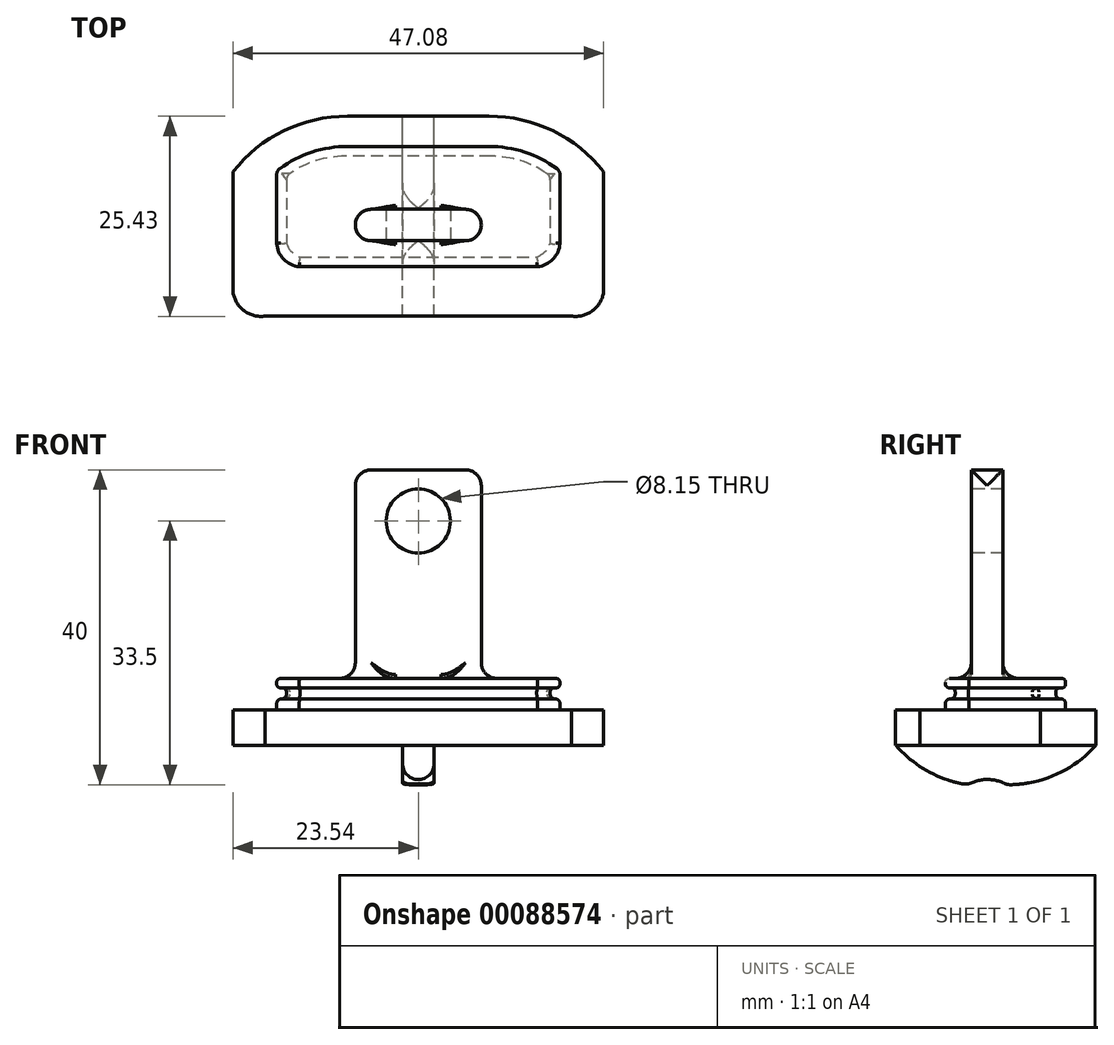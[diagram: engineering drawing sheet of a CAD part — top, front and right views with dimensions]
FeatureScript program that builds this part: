
annotation { "Feature Type Name" : "Feature", "Feature Type Description" : "" }
export const myFeature = defineFeature(function(context is Context, id is Id, definition is map)
    precondition{}
    {
        {
            var Q0;
            Q0=qCreatedBy(makeId("Top.planeOp"),FACE);
            var sketch = newSketch(context, id + "F0", { "sketchPlane" : qUnion([Q0])});
            skLineSegment(sketch, "E0", {"start": v(0, 17.58) * mm, "end": v(9, 17.58) * mm});
            skArc(sketch, "E1", {"start": v(23.54, 10.52) * mm, "mid": v(17.08, 15.72) * mm, "end": v(9, 17.58) * mm});
            skLineSegment(sketch, "E2.MirrorCS", {"start": v(0, 17.58) * mm, "end": v(-9, 17.58) * mm});
            skArc(sketch, "E3.MirrorCS", {"start": v(-23.54, 10.52) * mm, "mid": v(-17.08, 15.72) * mm, "end": v(-9, 17.58) * mm});
            skArc(sketch, "E4", {"start": v(19.44, -7.82) * mm, "mid": v(22.12, -7.14) * mm, "end": v(23.54, -4.76) * mm});
            skArc(sketch, "E5.MirrorCS", {"start": v(-19.44, -7.82) * mm, "mid": v(-22.12, -7.14) * mm, "end": v(-23.54, -4.76) * mm});
            skLineSegment(sketch, "E6", {"start": v(-23.54, 10.52) * mm, "end": v(-23.54, -4.76) * mm});
            skLineSegment(sketch, "E7", {"start": v(-19.44, -7.82) * mm, "end": v(19.44, -7.82) * mm});
            skLineSegment(sketch, "E8", {"start": v(23.54, -4.76) * mm, "end": v(23.54, 10.52) * mm});
            skLineSegment(sketch, "E9", {"start": v(0, 13.64) * mm, "end": v(9, 13.64) * mm});
            skArc(sketch, "E10", {"start": v(18, 10.52) * mm, "mid": v(13.76, 12.84) * mm, "end": v(9, 13.64) * mm});
            skLineSegment(sketch, "E11.MirrorCS", {"start": v(0, 13.64) * mm, "end": v(-9, 13.64) * mm});
            skArc(sketch, "E12.MirrorCS", {"start": v(-18, 10.52) * mm, "mid": v(-13.76, 12.84) * mm, "end": v(-9, 13.64) * mm});
            skArc(sketch, "E13", {"start": v(-18, 1.34) * mm, "mid": v(-17.1, -0.68) * mm, "end": v(-15.12, -1.65) * mm});
            skArc(sketch, "E14.MirrorCS", {"start": v(18, 1.34) * mm, "mid": v(17.1, -0.68) * mm, "end": v(15.12, -1.65) * mm});
            skLineSegment(sketch, "E15", {"start": v(-15.12, -1.65) * mm, "end": v(15.12, -1.65) * mm});
            skLineSegment(sketch, "E16", {"start": v(-18, 1.34) * mm, "end": v(-18, 10.52) * mm});
            skLineSegment(sketch, "E17", {"start": v(18, 10.52) * mm, "end": v(18, 1.34) * mm});
            skSolve(sketch);
        }
        {
            var Q0;
            Q0=makeQuery(id+"F0.imprint","IMPRINT",FACE,{"disambiguationData":[TD([[makeQuery(id+"F0.imprint","IMPRINT",EDGE,{"derivedFrom":sQuery(id+"F0.wireOp",EDGE,"E9")}),-1.0]])]});
            extrude(context, id + "F1", {"entities" : qUnion([Q0]), "depth" : 8.5 * mm});
        }
        {
            var Q0;
            Q0=qCreatedBy(makeId("Top.planeOp"),FACE);
            var sketch = newSketch(context, id + "F2", { "sketchPlane" : qUnion([Q0])});
            skLineSegment(sketch, "E18", {"start": v(0, 11.31) * mm, "end": v(9, 11.31) * mm});
            skArc(sketch, "E19", {"start": v(23.54, 4.25) * mm, "mid": v(17.08, 9.45) * mm, "end": v(9, 11.31) * mm});
            skLineSegment(sketch, "E20.MirrorCS", {"start": v(0, 11.31) * mm, "end": v(-9, 11.31) * mm});
            skArc(sketch, "E21.MirrorCS", {"start": v(-23.54, 4.25) * mm, "mid": v(-17.08, 9.45) * mm, "end": v(-9, 11.31) * mm});
            skArc(sketch, "E22", {"start": v(19.44, -14.09) * mm, "mid": v(22.12, -13.41) * mm, "end": v(23.54, -11.03) * mm});
            skArc(sketch, "E23.MirrorCS", {"start": v(-19.44, -14.09) * mm, "mid": v(-22.12, -13.41) * mm, "end": v(-23.54, -11.03) * mm});
            skLineSegment(sketch, "E24", {"start": v(-23.54, 4.25) * mm, "end": v(-23.54, -11.03) * mm});
            skLineSegment(sketch, "E25", {"start": v(-19.44, -14.09) * mm, "end": v(19.44, -14.09) * mm});
            skLineSegment(sketch, "E26", {"start": v(23.54, -11.03) * mm, "end": v(23.54, 4.25) * mm});
            skSolve(sketch);
        }
        {
            var Q0;
            Q0=makeQuery(id+"F1.opExtrude","SWEPT_BODY",BODY,{"disambiguationData":[OSD([sQuery(id+"F0.wireOp",EDGE,"E0"),sQuery(id+"F0.wireOp",EDGE,"E1"),sQuery(id+"F0.wireOp",EDGE,"E2.MirrorCS"),sQuery(id+"F0.wireOp",EDGE,"E3.MirrorCS"),sQuery(id+"F0.wireOp",EDGE,"E4"),sQuery(id+"F0.wireOp",EDGE,"E5.MirrorCS"),sQuery(id+"F0.wireOp",EDGE,"E6"),sQuery(id+"F0.wireOp",EDGE,"E7"),sQuery(id+"F0.wireOp",EDGE,"E8"),sQuery(id+"F0.wireOp",EDGE,"E9"),sQuery(id+"F0.wireOp",EDGE,"E10"),sQuery(id+"F0.wireOp",EDGE,"E11.MirrorCS"),sQuery(id+"F0.wireOp",EDGE,"E12.MirrorCS"),sQuery(id+"F0.wireOp",EDGE,"E13"),sQuery(id+"F0.wireOp",EDGE,"E14.MirrorCS"),sQuery(id+"F0.wireOp",EDGE,"E15"),sQuery(id+"F0.wireOp",EDGE,"E16"),sQuery(id+"F0.wireOp",EDGE,"E17")])]});
            var Q1;
            Q1=sQuery(id+"F2.wireOp",EDGE,"E26");
            transform(context, id + "F3", {"entities" : qUnion([Q0]), "transformType" : TransformType.TRANSLATION_DISTANCE, "transformDirection" : qUnion([Q1]), "distance" : 6.17 * mm, "oppositeDirection" : true, "makeCopy" : false});
        }
        {
            var Q0;
            Q0=qSketchRegion(id+"F2",true);
            extrude(context, id + "F4", {"entities" : qUnion([Q0]), "operationType" : NewBodyOperationType.ADD, "depth" : 4.5 * mm});
        }
        {
            var Q0;
            Q0=makeQuery(id+"F4.opExtrude","CAP_FACE",FACE,{"disambiguationData":[OSD([sQuery(id+"F2.wireOp",EDGE,"E18"),sQuery(id+"F2.wireOp",EDGE,"E19"),sQuery(id+"F2.wireOp",EDGE,"E20.MirrorCS"),sQuery(id+"F2.wireOp",EDGE,"E21.MirrorCS"),sQuery(id+"F2.wireOp",EDGE,"E22"),sQuery(id+"F2.wireOp",EDGE,"E23.MirrorCS"),sQuery(id+"F2.wireOp",EDGE,"E24"),sQuery(id+"F2.wireOp",EDGE,"E25"),sQuery(id+"F2.wireOp",EDGE,"E26")])],"isStart":false});
            var sketch = newSketch(context, id + "F5", { "sketchPlane" : qUnion([Q0])});
            skLineSegment(sketch, "E27", {"start": v(0, 6.22) * mm, "end": v(-9.3, 6.22) * mm});
            skLineSegment(sketch, "E28", {"start": v(0, -6.57) * mm, "end": v(-15.04, -6.57) * mm});
            skLineSegment(sketch, "E29.MirrorCS", {"start": v(0, 6.22) * mm, "end": v(9.3, 6.22) * mm});
            skLineSegment(sketch, "E30.MirrorCS", {"start": v(0, -6.57) * mm, "end": v(15.04, -6.57) * mm});
            skArc(sketch, "E31", {"start": v(-9.3, 6.22) * mm, "mid": v(-13.23, 5.58) * mm, "end": v(-16.75, 3.73) * mm});
            skArc(sketch, "E32", {"start": v(-16.75, -4.86) * mm, "mid": v(-16.1, -5.9) * mm, "end": v(-15.04, -6.57) * mm});
            skLineSegment(sketch, "E33", {"start": v(-16.75, 3.73) * mm, "end": v(-16.75, -4.86) * mm});
            skLineSegment(sketch, "E34.MirrorCS", {"start": v(16.75, 3.73) * mm, "end": v(16.75, -4.86) * mm});
            skArc(sketch, "E35.MirrorCS", {"start": v(9.3, 6.22) * mm, "mid": v(13.23, 5.58) * mm, "end": v(16.75, 3.73) * mm});
            skArc(sketch, "E36.MirrorCS", {"start": v(16.75, -4.86) * mm, "mid": v(16.1, -5.9) * mm, "end": v(15.04, -6.57) * mm});
            skLineSegment(sketch, "E37.bottom", {"start": v(18.45, -8.13) * mm, "end": v(-18.45, -8.13) * mm});
            skLineSegment(sketch, "E37.top", {"start": v(18.45, 8.13) * mm, "end": v(-18.45, 8.13) * mm});
            skLineSegment(sketch, "E37.left", {"start": v(18.45, -8.13) * mm, "end": v(18.45, 8.13) * mm});
            skLineSegment(sketch, "E37.right", {"start": v(-18.45, -8.13) * mm, "end": v(-18.45, 8.13) * mm});
            skPoint(sketch, "E37.middle", {"position": v(0, 0) * mm});
            skSolve(sketch);
        }
        {
            var Q0;
            Q0=qSketchRegion(id+"F5",true);
            extrude(context, id + "F6", {"entities" : qUnion([Q0]), "operationType" : NewBodyOperationType.REMOVE, "depth" : 2.8 * mm, "hasSecondDirection" : true, "secondDirectionOppositeDirection" : false, "secondDirectionDepth" : 1.4 * mm});
        }
        {
            var Q0;
            Q0=makeQuery(id+"F1.opExtrude","CAP_FACE",FACE,{"disambiguationData":[OSD([sQuery(id+"F0.wireOp",EDGE,"E9"),sQuery(id+"F0.wireOp",EDGE,"E10"),sQuery(id+"F0.wireOp",EDGE,"E11.MirrorCS"),sQuery(id+"F0.wireOp",EDGE,"E12.MirrorCS"),sQuery(id+"F0.wireOp",EDGE,"E13"),sQuery(id+"F0.wireOp",EDGE,"E14.MirrorCS"),sQuery(id+"F0.wireOp",EDGE,"E15"),sQuery(id+"F0.wireOp",EDGE,"E16"),sQuery(id+"F0.wireOp",EDGE,"E17")])],"isStart":false});
            var sketch = newSketch(context, id + "F7", { "sketchPlane" : qUnion([Q0])});
            skLineSegment(sketch, "E38.rect.bottom", {"start": v(8, -4.51) * mm, "end": v(-8, -4.51) * mm});
            skLineSegment(sketch, "E38.rect.top", {"start": v(8, -0.51) * mm, "end": v(-8, -0.51) * mm});
            skLineSegment(sketch, "E38.rect.left", {"start": v(8, -4.51) * mm, "end": v(8, -0.51) * mm});
            skLineSegment(sketch, "E38.rect.right", {"start": v(-8, -4.51) * mm, "end": v(-8, -0.51) * mm});
            skPoint(sketch, "E38.rect.middle", {"position": v(0, -2.51) * mm});
            skSolve(sketch);
        }
        {
            var Q0;
            Q0=qSketchRegion(id+"F7",true);
            extrude(context, id + "F8", {"entities" : qUnion([Q0]), "operationType" : NewBodyOperationType.ADD, "depth" : 26.5 * mm});
        }
        {
            var Q0;
            Q0=makeQuery(id+"F8.opExtrude","SWEPT_FACE",FACE,{"disambiguationData":[OSD([sQuery(id+"F7.wireOp",EDGE,"E38.rect.bottom")])]});
            var sketch = newSketch(context, id + "F9", { "sketchPlane" : qUnion([Q0])});
            skCircle(sketch, "E39", {"center": v(0, 28.5) * mm, "radius": 4.08 * mm});
            skSolve(sketch);
        }
        {
            var Q0;
            Q0=qSketchRegion(id+"F9",true);
            extrude(context, id + "F10", {"entities" : qUnion([Q0]), "operationType" : NewBodyOperationType.REMOVE, "endBound" : BoundingType.UP_TO_NEXT, "oppositeDirection" : true, "depth" : 25 * mm});
        }
        {
            var Q0;
            {var subQ0=sQuery(id+"F0.wireOp",EDGE,"E10");var subQ1=sQuery(id+"F0.wireOp",EDGE,"E17");Q0=makeQuery(id+"F6.boolean.opBoolean","SPLIT",EDGE,{"disambiguationData":[TD([makeQuery(id+"F4.opExtrude","CAP_FACE",FACE,{"disambiguationData":[OSD([sQuery(id+"F2.wireOp",EDGE,"E18"),sQuery(id+"F2.wireOp",EDGE,"E19"),sQuery(id+"F2.wireOp",EDGE,"E20.MirrorCS"),sQuery(id+"F2.wireOp",EDGE,"E21.MirrorCS"),sQuery(id+"F2.wireOp",EDGE,"E22"),sQuery(id+"F2.wireOp",EDGE,"E23.MirrorCS"),sQuery(id+"F2.wireOp",EDGE,"E24"),sQuery(id+"F2.wireOp",EDGE,"E25"),sQuery(id+"F2.wireOp",EDGE,"E26")])],"isStart":false})])],"derivedFrom":makeQuery(id+"F1.opExtrude","SWEPT_EDGE",EDGE,{"disambiguationData":[OSD([subQ0,subQ1])]})});}
            var Q1;
            {var subQ0=sQuery(id+"F0.wireOp",EDGE,"E17");var subQ1=sQuery(id+"F0.wireOp",EDGE,"E10");Q1=makeQuery(id+"F6.boolean.opBoolean","SPLIT",EDGE,{"disambiguationData":[TD([makeQuery(id+"F1.opExtrude","CAP_FACE",FACE,{"disambiguationData":[OSD([sQuery(id+"F0.wireOp",EDGE,"E9"),subQ1,sQuery(id+"F0.wireOp",EDGE,"E11.MirrorCS"),sQuery(id+"F0.wireOp",EDGE,"E12.MirrorCS"),sQuery(id+"F0.wireOp",EDGE,"E13"),sQuery(id+"F0.wireOp",EDGE,"E14.MirrorCS"),sQuery(id+"F0.wireOp",EDGE,"E15"),sQuery(id+"F0.wireOp",EDGE,"E16"),subQ0])],"isStart":false})])],"derivedFrom":makeQuery(id+"F1.opExtrude","SWEPT_EDGE",EDGE,{"disambiguationData":[OSD([subQ1,subQ0])]})});}
            var Q2;
            {var subQ0=sQuery(id+"F0.wireOp",EDGE,"E12.MirrorCS");var subQ1=sQuery(id+"F0.wireOp",EDGE,"E16");Q2=makeQuery(id+"F6.boolean.opBoolean","SPLIT",EDGE,{"disambiguationData":[TD([makeQuery(id+"F4.opExtrude","CAP_FACE",FACE,{"disambiguationData":[OSD([sQuery(id+"F2.wireOp",EDGE,"E18"),sQuery(id+"F2.wireOp",EDGE,"E19"),sQuery(id+"F2.wireOp",EDGE,"E20.MirrorCS"),sQuery(id+"F2.wireOp",EDGE,"E21.MirrorCS"),sQuery(id+"F2.wireOp",EDGE,"E22"),sQuery(id+"F2.wireOp",EDGE,"E23.MirrorCS"),sQuery(id+"F2.wireOp",EDGE,"E24"),sQuery(id+"F2.wireOp",EDGE,"E25"),sQuery(id+"F2.wireOp",EDGE,"E26")])],"isStart":false})])],"derivedFrom":makeQuery(id+"F1.opExtrude","SWEPT_EDGE",EDGE,{"disambiguationData":[OSD([subQ0,subQ1])]})});}
            var Q3;
            {var subQ0=sQuery(id+"F0.wireOp",EDGE,"E16");var subQ1=sQuery(id+"F0.wireOp",EDGE,"E12.MirrorCS");Q3=makeQuery(id+"F6.boolean.opBoolean","SPLIT",EDGE,{"disambiguationData":[TD([makeQuery(id+"F1.opExtrude","CAP_FACE",FACE,{"disambiguationData":[OSD([sQuery(id+"F0.wireOp",EDGE,"E9"),sQuery(id+"F0.wireOp",EDGE,"E10"),sQuery(id+"F0.wireOp",EDGE,"E11.MirrorCS"),subQ1,sQuery(id+"F0.wireOp",EDGE,"E13"),sQuery(id+"F0.wireOp",EDGE,"E14.MirrorCS"),sQuery(id+"F0.wireOp",EDGE,"E15"),subQ0,sQuery(id+"F0.wireOp",EDGE,"E17")])],"isStart":false})])],"derivedFrom":makeQuery(id+"F1.opExtrude","SWEPT_EDGE",EDGE,{"disambiguationData":[OSD([subQ1,subQ0])]})});}
            fillet(context, id + "F11", {"entities" : qUnion([Q0, Q1, Q2, Q3]), "radius" : 1 * mm, "tangentPropagation" : true, "allowEdgeOverflow" : false});
        }
        {
            var Q0;
            Q0=makeQuery(id+"F8.opExtrude","SWEPT_FACE",FACE,{"disambiguationData":[OSD([sQuery(id+"F7.wireOp",EDGE,"E38.rect.left")])]});
            var Q1;
            Q1=makeQuery(id+"F8.opExtrude","SWEPT_FACE",FACE,{"disambiguationData":[OSD([sQuery(id+"F7.wireOp",EDGE,"E38.rect.right")])]});
            fillet(context, id + "F12", {"entities" : qUnion([Q0, Q1]), "radius" : 2 * mm, "tangentPropagation" : true, "allowEdgeOverflow" : false});
        }
        {
            var Q0;
            Q0=makeQuery(id+"F6.boolean.opBoolean","COPY",FACE,{"derivedFrom":makeQuery(id+"F6.opExtrude","CAP_FACE",FACE,{"disambiguationData":[OSD([sQuery(id+"F5.wireOp",EDGE,"E27"),sQuery(id+"F5.wireOp",EDGE,"E28"),sQuery(id+"F5.wireOp",EDGE,"E29.MirrorCS"),sQuery(id+"F5.wireOp",EDGE,"E30.MirrorCS"),sQuery(id+"F5.wireOp",EDGE,"E31"),sQuery(id+"F5.wireOp",EDGE,"E32"),sQuery(id+"F5.wireOp",EDGE,"E33"),sQuery(id+"F5.wireOp",EDGE,"E34.MirrorCS"),sQuery(id+"F5.wireOp",EDGE,"E35.MirrorCS"),sQuery(id+"F5.wireOp",EDGE,"E36.MirrorCS"),sQuery(id+"F5.wireOp",EDGE,"E37.bottom"),sQuery(id+"F5.wireOp",EDGE,"E37.top"),sQuery(id+"F5.wireOp",EDGE,"E37.left"),sQuery(id+"F5.wireOp",EDGE,"E37.right")])],"isStart":true})});
            fillet(context, id + "F13", {"entities" : qUnion([Q0]), "radius" : .6 * mm, "tangentPropagation" : true, "allowEdgeOverflow" : false});
        }
        {
            var Q0;
            Q0=makeQuery(id+"F6.boolean.opBoolean","COPY",FACE,{"derivedFrom":makeQuery(id+"F6.opExtrude","CAP_FACE",FACE,{"disambiguationData":[OSD([sQuery(id+"F5.wireOp",EDGE,"E27"),sQuery(id+"F5.wireOp",EDGE,"E28"),sQuery(id+"F5.wireOp",EDGE,"E29.MirrorCS"),sQuery(id+"F5.wireOp",EDGE,"E30.MirrorCS"),sQuery(id+"F5.wireOp",EDGE,"E31"),sQuery(id+"F5.wireOp",EDGE,"E32"),sQuery(id+"F5.wireOp",EDGE,"E33"),sQuery(id+"F5.wireOp",EDGE,"E34.MirrorCS"),sQuery(id+"F5.wireOp",EDGE,"E35.MirrorCS"),sQuery(id+"F5.wireOp",EDGE,"E36.MirrorCS"),sQuery(id+"F5.wireOp",EDGE,"E37.bottom"),sQuery(id+"F5.wireOp",EDGE,"E37.top"),sQuery(id+"F5.wireOp",EDGE,"E37.left"),sQuery(id+"F5.wireOp",EDGE,"E37.right")])],"isStart":false})});
            fillet(context, id + "F14", {"entities" : qUnion([Q0]), "radius" : .5 * mm, "tangentPropagation" : true, "allowEdgeOverflow" : false});
        }
        {
            var Q0;
            Q0=makeQuery(id+"F14.opFillet","BLEND_EDGE",EDGE,{"blendedFrom":[makeQuery(id+"F6.boolean.opBoolean","COPY",EDGE,{"derivedFrom":makeQuery(id+"F6.opExtrude","CAP_EDGE",EDGE,{"disambiguationData":[OSD([sQuery(id+"F5.wireOp",EDGE,"E34.MirrorCS")])],"isStart":false})}),makeQuery(id+"F6.boolean.opBoolean","COPY",EDGE,{"derivedFrom":makeQuery(id+"F6.opExtrude","CAP_EDGE",EDGE,{"disambiguationData":[OSD([sQuery(id+"F5.wireOp",EDGE,"E35.MirrorCS")])],"isStart":false})})],"blendedInto":[]});
            var Q1;
            Q1=makeQuery(id+"F14.opFillet","BLEND_EDGE",EDGE,{"blendedFrom":[makeQuery(id+"F6.boolean.opBoolean","COPY",EDGE,{"derivedFrom":makeQuery(id+"F6.opExtrude","CAP_EDGE",EDGE,{"disambiguationData":[OSD([sQuery(id+"F5.wireOp",EDGE,"E31")])],"isStart":false})}),makeQuery(id+"F6.boolean.opBoolean","COPY",EDGE,{"derivedFrom":makeQuery(id+"F6.opExtrude","CAP_EDGE",EDGE,{"disambiguationData":[OSD([sQuery(id+"F5.wireOp",EDGE,"E33")])],"isStart":false})})],"blendedInto":[]});
            fillet(context, id + "F15", {"entities" : qUnion([Q0, Q1]), "radius" : 1 * mm, "tangentPropagation" : true, "allowEdgeOverflow" : false});
        }
        {
            var Q0;
            Q0=makeQuery(id+"F1.opExtrude","CAP_FACE",FACE,{"disambiguationData":[OSD([sQuery(id+"F0.wireOp",EDGE,"E9"),sQuery(id+"F0.wireOp",EDGE,"E10"),sQuery(id+"F0.wireOp",EDGE,"E11.MirrorCS"),sQuery(id+"F0.wireOp",EDGE,"E12.MirrorCS"),sQuery(id+"F0.wireOp",EDGE,"E13"),sQuery(id+"F0.wireOp",EDGE,"E14.MirrorCS"),sQuery(id+"F0.wireOp",EDGE,"E15"),sQuery(id+"F0.wireOp",EDGE,"E16"),sQuery(id+"F0.wireOp",EDGE,"E17")])],"isStart":false});
            fillet(context, id + "F16", {"entities" : qUnion([Q0]), "radius" : .5 * mm, "tangentPropagation" : true, "allowEdgeOverflow" : false});
        }
        {
            var Q0;
            Q0=qCreatedBy(makeId("Right.planeOp"),FACE);
            var sketch = newSketch(context, id + "F17", { "sketchPlane" : qUnion([Q0])});
            skLineSegment(sketch, "E40.bottom", {"start": v(-14.09, 0) * mm, "end": v(11.31, 0) * mm});
            skLineSegment(sketch, "E40.top", {"start": v(-14.09, -5) * mm, "end": v(11.31, -5) * mm});
            skLineSegment(sketch, "E40.left", {"start": v(-14.09, 0) * mm, "end": v(-14.09, -5) * mm});
            skLineSegment(sketch, "E40.right", {"start": v(11.31, 0) * mm, "end": v(11.31, -5) * mm});
            skArc(sketch, "E41", {"start": v(0, -5) * mm, "mid": v(-2.5, -4.33) * mm, "end": v(-5, -5) * mm});
            skArc(sketch, "E42", {"start": v(-14.09, 0) * mm, "mid": v(-9.98, -3.31) * mm, "end": v(-5, -5) * mm});
            skArc(sketch, "E43", {"start": v(0, -5) * mm, "mid": v(6.2, -3.72) * mm, "end": v(11.31, 0) * mm});
            skSolve(sketch);
        }
        {
            var Q0;
            Q0=makeQuery(id+"F17.imprint","IMPRINT",FACE,{"disambiguationData":[TD([[makeQuery(id+"F17.imprint","IMPRINT",EDGE,{"derivedFrom":sQuery(id+"F17.wireOp",EDGE,"E40.bottom")}),-1.0]])]});
            extrude(context, id + "F18", {"entities" : qUnion([Q0]), "operationType" : NewBodyOperationType.ADD, "depth" : 2 * mm, "hasSecondDirection" : true, "secondDirectionOppositeDirection" : true, "secondDirectionDepth" : 2 * mm});
        }
        {
            var Q0;
            Q0=makeQuery(id+"F18.opExtrude","SWEPT_FACE",FACE,{"disambiguationData":[OSD([sQuery(id+"F17.wireOp",EDGE,"E41")])]});
            var Q1;
            Q1=makeQuery(id+"F18.opExtrude","CAP_EDGE",EDGE,{"disambiguationData":[OSD([sQuery(id+"F17.wireOp",EDGE,"E40.bottom")])],"isStart":true});
            var Q2;
            Q2=makeQuery(id+"F18.opExtrude","CAP_EDGE",EDGE,{"disambiguationData":[OSD([sQuery(id+"F17.wireOp",EDGE,"E40.bottom")])],"isStart":false});
            fillet(context, id + "F19", {"entities" : qUnion([Q0, Q1, Q2]), "radius" : 2 * mm, "tangentPropagation" : true, "allowEdgeOverflow" : false});
        }
    });
